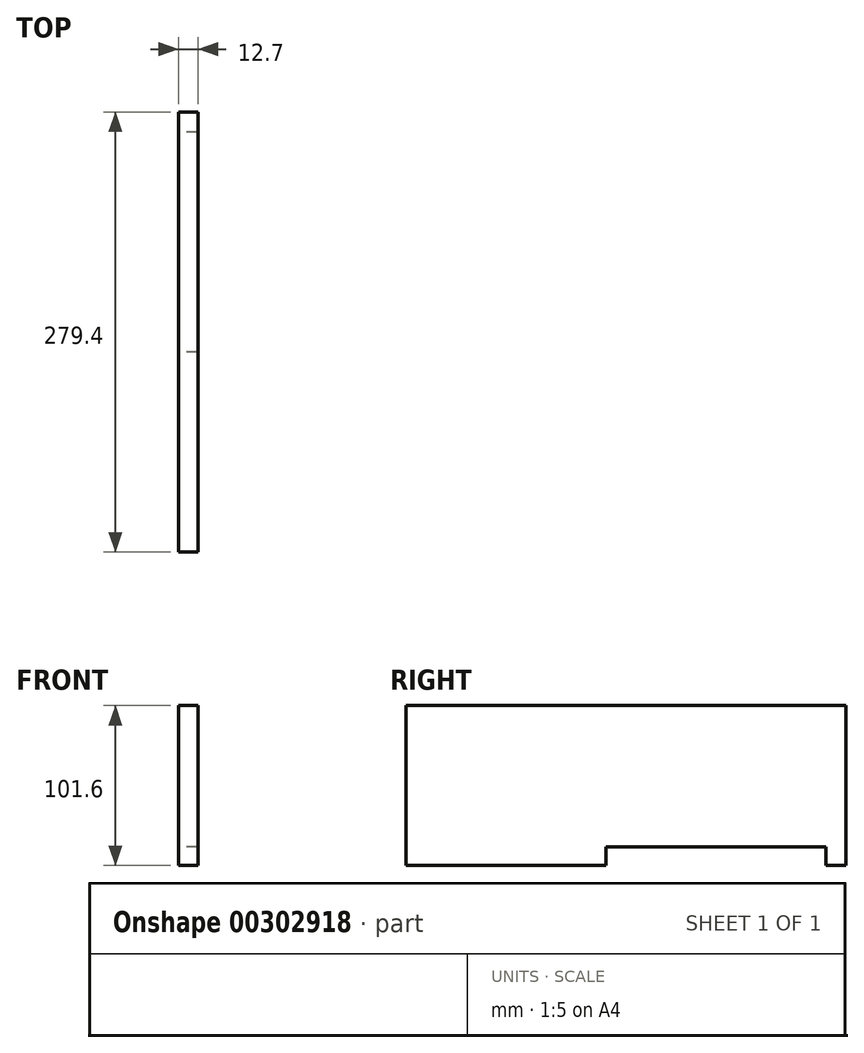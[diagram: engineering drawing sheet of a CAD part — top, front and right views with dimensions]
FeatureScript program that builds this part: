
annotation { "Feature Type Name" : "Feature", "Feature Type Description" : "" }
export const myFeature = defineFeature(function(context is Context, id is Id, definition is map)
    precondition{}
    {
        {
            var Q0;
            Q0=qCreatedBy(makeId("Right.planeOp"),FACE);
            var sketch = newSketch(context, id + "F0", { "sketchPlane" : qUnion([Q0])});
            skLineSegment(sketch, "E0.bottom", {"start": v(139.7, 50.8) * mm, "end": v(-139.7, 50.8) * mm});
            skLineSegment(sketch, "E0.top", {"start": v(139.7, -50.8) * mm, "end": v(-139.7, -50.8) * mm});
            skLineSegment(sketch, "E0.left", {"start": v(139.7, 50.8) * mm, "end": v(139.7, -50.8) * mm});
            skLineSegment(sketch, "E0.right", {"start": v(-139.7, 50.8) * mm, "end": v(-139.7, -50.8) * mm});
            skPoint(sketch, "E0.middle", {"position": v(0, 0) * mm});
            skLineSegment(sketch, "E1", {"start": v(127, -50.8) * mm, "end": v(127, -39) * mm});
            skLineSegment(sketch, "E2", {"start": v(127, -39) * mm, "end": v(-12.7, -39) * mm});
            skLineSegment(sketch, "E3", {"start": v(-12.7, -39) * mm, "end": v(-12.7, -50.8) * mm});
            skSolve(sketch);
        }
        {
            var Q0;
            Q0=makeQuery(id+"F0.imprint","IMPRINT",FACE,{"disambiguationData":[TD([[makeQuery(id+"F0.imprint","IMPRINT",EDGE,{"derivedFrom":sQuery(id+"F0.wireOp",EDGE,"E0.bottom")}),1.0]])]});
            extrude(context, id + "F1", {"entities" : qUnion([Q0]), "depth" : 12.7 * mm});
        }
    });
